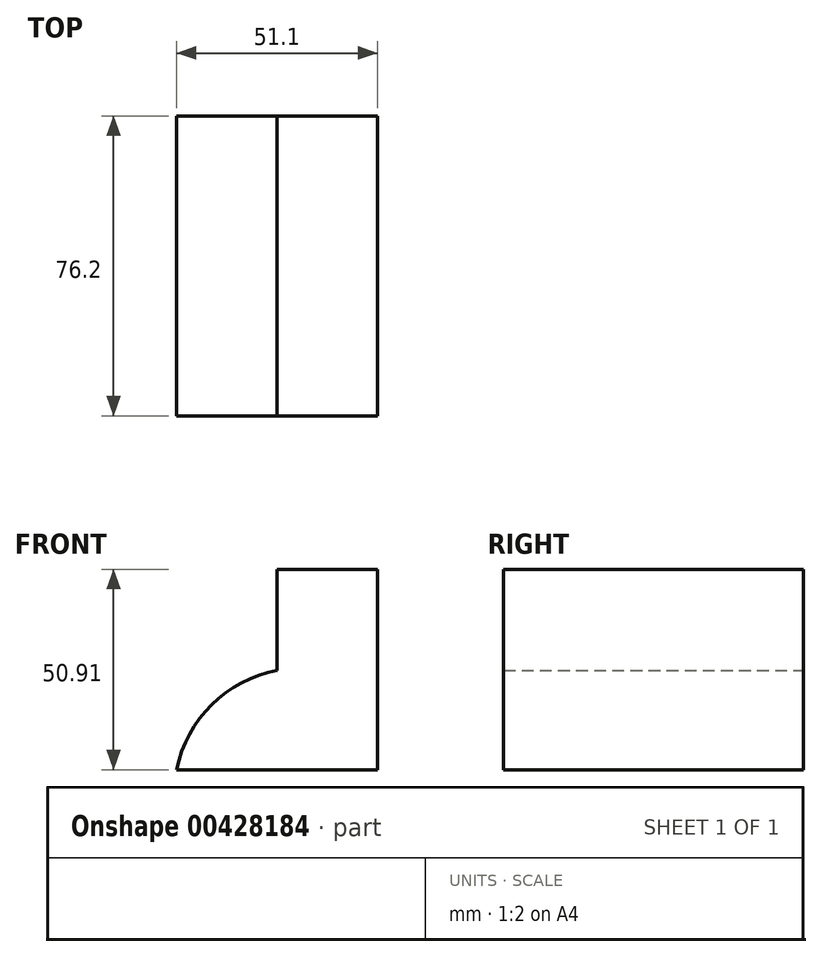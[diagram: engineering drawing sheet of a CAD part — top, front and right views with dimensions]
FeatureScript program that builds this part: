
annotation { "Feature Type Name" : "Feature", "Feature Type Description" : "" }
export const myFeature = defineFeature(function(context is Context, id is Id, definition is map)
    precondition{}
    {
        {
            var Q0;
            Q0=qCreatedBy(makeId("Front.planeOp"),FACE);
            var sketch = newSketch(context, id + "F0", { "sketchPlane" : qUnion([Q0])});
            skLineSegment(sketch, "E0", {"start": v(0, 0) * mm, "end": v(0, 25.65) * mm});
            skLineSegment(sketch, "E1", {"start": v(0, 25.65) * mm, "end": v(25.55, 25.65) * mm});
            skLineSegment(sketch, "E2", {"start": v(25.55, 25.65) * mm, "end": v(25.55, -25.26) * mm});
            skLineSegment(sketch, "E3", {"start": v(25.55, -25.26) * mm, "end": v(-25.55, -25.26) * mm});
            skArc(sketch, "E4", {"start": v(0, 0) * mm, "mid": v(-16.6, -8.75) * mm, "end": v(-25.55, -25.26) * mm});
            skSolve(sketch);
        }
        {
            var Q0;
            Q0=makeQuery(id+"F0.imprint","IMPRINT",FACE,{"disambiguationData":[TD([[makeQuery(id+"F0.imprint","IMPRINT",EDGE,{"derivedFrom":sQuery(id+"F0.wireOp",EDGE,"E0")}),-1.0]])]});
            extrude(context, id + "F1", {"entities" : qUnion([Q0]), "depth" : 76.2 * mm});
        }
    });
